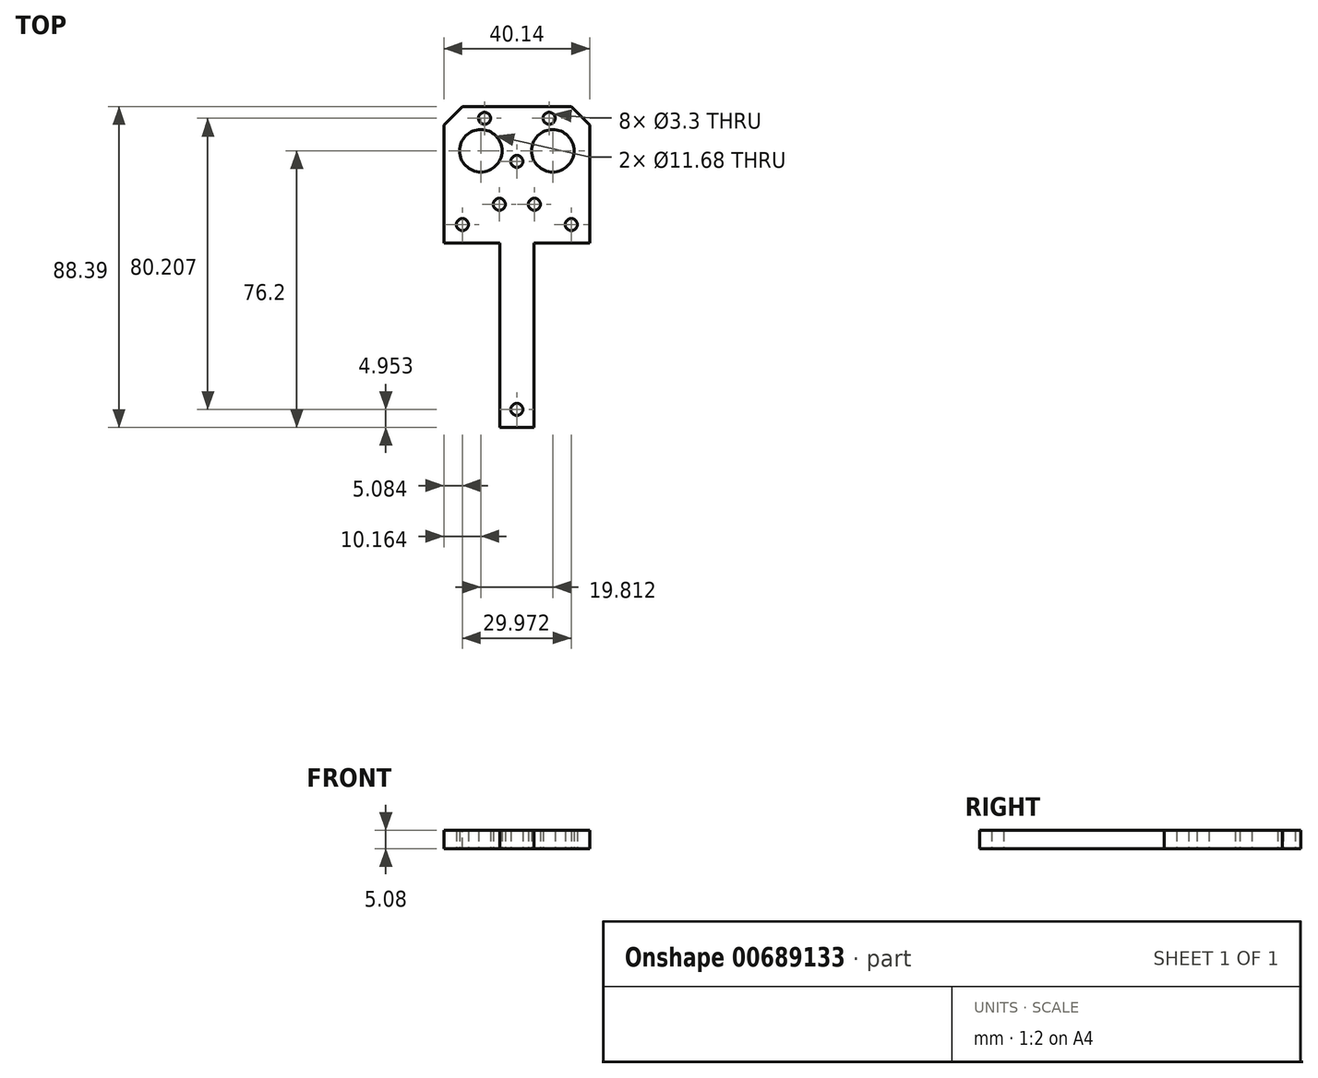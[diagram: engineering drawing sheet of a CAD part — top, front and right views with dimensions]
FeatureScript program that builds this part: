
annotation { "Feature Type Name" : "Feature", "Feature Type Description" : "" }
export const myFeature = defineFeature(function(context is Context, id is Id, definition is map)
    precondition{}
    {
        {
            var Q0;
            Q0=qCreatedBy(makeId("Top.planeOp"),FACE);
            var sketch = newSketch(context, id + "F0", { "sketchPlane" : qUnion([Q0])});
            skLineSegment(sketch, "E0.bottom", {"start": v(-20.07, 0) * mm, "end": v(-4.7, 0) * mm});
            skLineSegment(sketch, "E0.top", {"start": v(-20.07, 37.6) * mm, "end": v(20.07, 37.6) * mm});
            skLineSegment(sketch, "E0.left", {"start": v(-20.07, 0) * mm, "end": v(-20.07, 37.6) * mm});
            skLineSegment(sketch, "E0.right", {"start": v(20.07, 0) * mm, "end": v(20.07, 37.6) * mm});
            skPoint(sketch, "E0.middle", {"position": v(0, 18.8) * mm});
            skLineSegment(sketch, "E1.bottom", {"start": v(-4.7, -50.8) * mm, "end": v(4.7, -50.8) * mm});
            skLineSegment(sketch, "E1.left", {"start": v(-4.7, -50.8) * mm, "end": v(-4.7, 0) * mm});
            skLineSegment(sketch, "E1.right", {"start": v(4.7, -50.8) * mm, "end": v(4.7, 0) * mm});
            skPoint(sketch, "E1.middle", {"position": v(0, 0) * mm});
            skPoint(sketch, "E1.top.start.orphan", {"position": v(-4.7, 50.8) * mm});
            skPoint(sketch, "E2.orphan", {"position": v(4.7, 50.8) * mm});
            skCircle(sketch, "E3", {"center": v(0, -45.85) * mm, "radius": 1.65 * mm});
            skCircle(sketch, "E4", {"center": v(0, 22.48) * mm, "radius": 1.65 * mm});
            skCircle(sketch, "E5", {"center": v(9.9, 25.4) * mm, "radius": 5.84 * mm});
            skCircle(sketch, "E6", {"center": v(8.89, 34.36) * mm, "radius": 1.65 * mm});
            skCircle(sketch, "E7", {"center": v(14.99, 5.08) * mm, "radius": 1.65 * mm});
            skLineSegment(sketch, "E8.trimOffspring", {"start": v(4.7, 0) * mm, "end": v(20.07, 0) * mm});
            skCircle(sketch, "E9.MirrorC", {"center": v(-8.89, 34.36) * mm, "radius": 1.65 * mm});
            skCircle(sketch, "E10.MirrorC", {"center": v(-9.9, 25.4) * mm, "radius": 5.84 * mm});
            skCircle(sketch, "E11.MirrorC", {"center": v(-14.99, 5.08) * mm, "radius": 1.65 * mm});
            skCircle(sketch, "E12", {"center": v(4.83, 10.67) * mm, "radius": 1.65 * mm});
            skCircle(sketch, "E13.MirrorC", {"center": v(-4.83, 10.67) * mm, "radius": 1.65 * mm});
            skSolve(sketch);
        }
        {
            var Q0;
            Q0=makeQuery(id+"F0.imprint","IMPRINT",FACE,{"disambiguationData":[TD([[makeQuery(id+"F0.imprint","IMPRINT",EDGE,{"derivedFrom":sQuery(id+"F0.wireOp",EDGE,"E0.bottom")}),1.0]])]});
            extrude(context, id + "F1", {"entities" : qUnion([Q0]), "depth" : 5.08 * mm, "offsetDistance" : 25.4 * mm});
        }
        {
            var Q0;
            Q0=makeQuery(id+"F1.opExtrude","SWEPT_EDGE",EDGE,{"disambiguationData":[OSD([sQuery(id+"F0.wireOp",EDGE,"E0.top"),sQuery(id+"F0.wireOp",EDGE,"E0.left")])]});
            var Q1;
            Q1=makeQuery(id+"F1.opExtrude","SWEPT_EDGE",EDGE,{"disambiguationData":[OSD([sQuery(id+"F0.wireOp",EDGE,"E0.top"),sQuery(id+"F0.wireOp",EDGE,"E0.right")])]});
            chamfer(context, id + "F2", {"entities" : qUnion([Q0, Q1]), "width" : 5.08 * mm, "tangentPropagation" : true});
        }
    });
